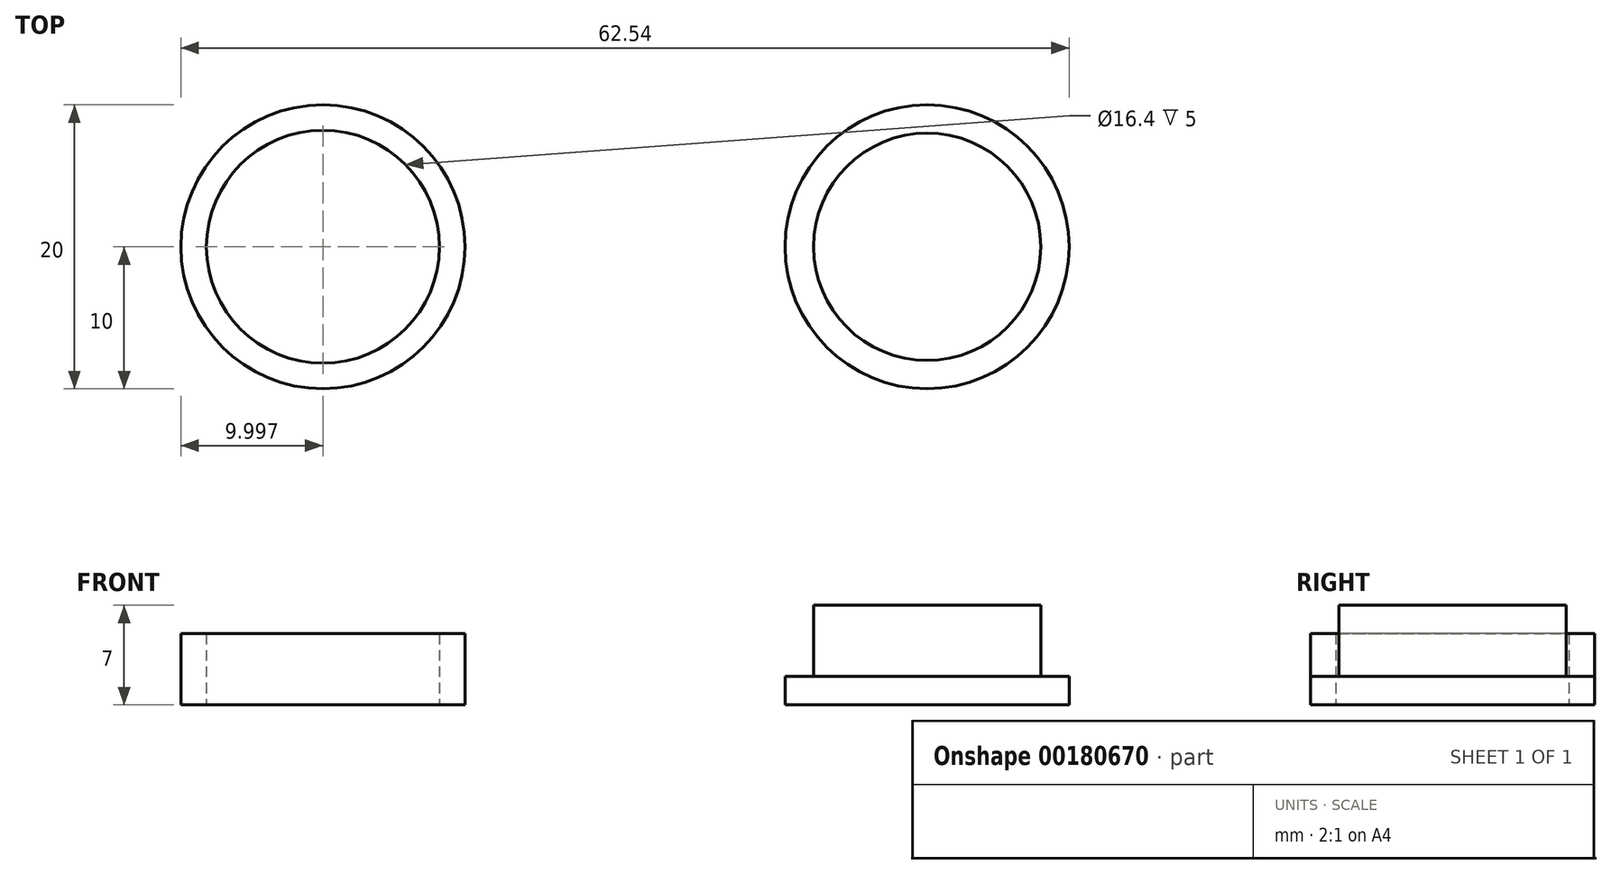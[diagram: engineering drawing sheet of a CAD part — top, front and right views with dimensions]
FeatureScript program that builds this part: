
annotation { "Feature Type Name" : "Feature", "Feature Type Description" : "" }
export const myFeature = defineFeature(function(context is Context, id is Id, definition is map)
    precondition{}
    {
        {
            var Q0;
            Q0=qCreatedBy(makeId("Front.planeOp"),FACE);
            var sketch = newSketch(context, id + "F0", { "sketchPlane" : qUnion([Q0])});
            skLineSegment(sketch, "E0", {"start": v(0, 0) * mm, "end": v(-10, 0) * mm});
            skLineSegment(sketch, "E1", {"start": v(-10, 0) * mm, "end": v(-10, 2) * mm});
            skLineSegment(sketch, "E2", {"start": v(-10, 2) * mm, "end": v(-8, 2) * mm});
            skLineSegment(sketch, "E3", {"start": v(-8, 2) * mm, "end": v(-8, 7) * mm});
            skLineSegment(sketch, "E4", {"start": v(-8, 7) * mm, "end": v(0, 7) * mm});
            skLineSegment(sketch, "E5", {"start": v(0, 7) * mm, "end": v(0, 0) * mm});
            skSolve(sketch);
        }
        {
            var Q0;
            Q0=makeQuery(id+"F0.imprint","IMPRINT",FACE,{"disambiguationData":[TD([[makeQuery(id+"F0.imprint","IMPRINT",EDGE,{"derivedFrom":sQuery(id+"F0.wireOp",EDGE,"E0")}),-1.0]])]});
            var Q1;
            Q1=sQuery(id+"F0.wireOp",EDGE,"E5");
            revolve(context, id + "F1", {"entities" : qUnion([Q0]), "axis" : qUnion([Q1]), "revolveType" : RevolveType.FULL});
        }
        {
            var Q0;
            Q0=qCreatedBy(makeId("Top.planeOp"),FACE);
            var sketch = newSketch(context, id + "F2", { "sketchPlane" : qUnion([Q0])});
            skCircle(sketch, "E6", {"center": v(-42.54, 0) * mm, "radius": 10 * mm});
            skCircle(sketch, "E7", {"center": v(-42.54, 0) * mm, "radius": 8.2 * mm});
            skSolve(sketch);
        }
        {
            var Q0;
            Q0=makeQuery(id+"F2.imprint","IMPRINT",FACE,{"disambiguationData":[TD([[makeQuery(id+"F2.imprint","IMPRINT",EDGE,{"derivedFrom":sQuery(id+"F2.wireOp",EDGE,"E6")}),1.0]])]});
            extrude(context, id + "F3", {"entities" : qUnion([Q0]), "depth" : 5 * mm});
        }
    });
